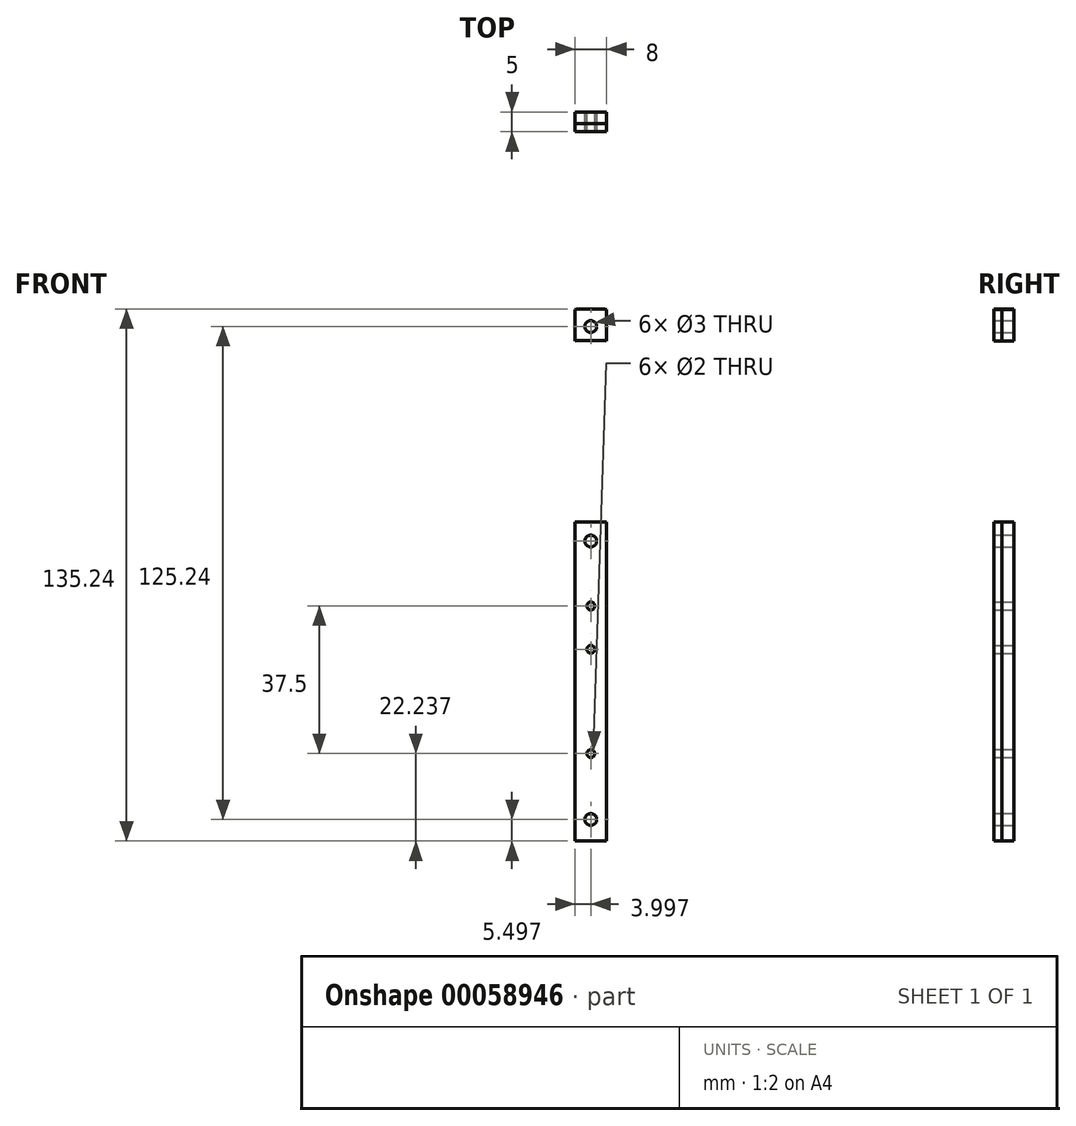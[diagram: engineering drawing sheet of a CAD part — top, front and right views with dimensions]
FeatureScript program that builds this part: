
annotation { "Feature Type Name" : "Feature", "Feature Type Description" : "" }
export const myFeature = defineFeature(function(context is Context, id is Id, definition is map)
    precondition{}
    {
        {
            var Q0;
            Q0=qCreatedBy(makeId("Front.planeOp"),FACE);
            var sketch = newSketch(context, id + "F0", { "sketchPlane" : qUnion([Q0])});
            skCircle(sketch, "E0", {"center": v(3.93, 28.4) * mm, "radius": 1.5 * mm});
            skLineSegment(sketch, "E1", {"start": v(7.05, 28.4) * mm, "end": v(-45.07, 28.4) * mm, "construction": true});
            skLineSegment(sketch, "E2", {"start": v(3.93, 33.22) * mm, "end": v(3.93, -47.83) * mm, "construction": true});
            skCircle(sketch, "E3", {"center": v(-34.07, 28.4) * mm, "radius": 1 * mm});
            skLineSegment(sketch, "E4", {"start": v(2.93, 11.9) * mm, "end": v(4.93, 11.9) * mm, "construction": true});
            skLineSegment(sketch, "E5", {"start": v(2.93, 0.9) * mm, "end": v(4.93, 0.9) * mm, "construction": true});
            skCircle(sketch, "E6", {"center": v(3.93, 0.9) * mm, "radius": 1 * mm});
            skLineSegment(sketch, "E7", {"start": v(2.93, -25.6) * mm, "end": v(4.93, -25.6) * mm, "construction": true});
            skCircle(sketch, "E8", {"center": v(3.93, -25.6) * mm, "radius": 1 * mm});
            skCircle(sketch, "E9", {"center": v(3.93, 11.9) * mm, "radius": 1 * mm});
            skPoint(sketch, "E10", {"position": v(3.93, -42.33) * mm});
            skCircle(sketch, "E11", {"center": v(3.93, -42.33) * mm, "radius": 1.5 * mm});
            skLineSegment(sketch, "E12.bottom", {"start": v(-0.07, 33.22) * mm, "end": v(7.93, 33.22) * mm});
            skLineSegment(sketch, "E12.top", {"start": v(-0.07, -47.83) * mm, "end": v(7.93, -47.83) * mm});
            skLineSegment(sketch, "E12.left", {"start": v(-0.07, 33.22) * mm, "end": v(-0.07, -47.83) * mm});
            skLineSegment(sketch, "E12.right", {"start": v(7.93, 33.22) * mm, "end": v(7.93, -47.83) * mm});
            skLineSegment(sketch, "E13.top", {"start": v(-0.07, 87.4) * mm, "end": v(7.93, 87.4) * mm});
            skLineSegment(sketch, "E13.left", {"start": v(-0.07, 33.22) * mm, "end": v(-0.07, 87.4) * mm});
            skLineSegment(sketch, "E13.right", {"start": v(7.93, 33.22) * mm, "end": v(7.93, 87.4) * mm});
            skPoint(sketch, "E14", {"position": v(3.93, 87.4) * mm});
            skCircle(sketch, "E15", {"center": v(3.93, 82.9) * mm, "radius": 1.5 * mm});
            skLineSegment(sketch, "E16", {"start": v(-0.07, 79.4) * mm, "end": v(7.93, 79.4) * mm, "construction": true});
            skCircle(sketch, "E17", {"center": v(3.93, 28.4) * mm, "radius": 59 * mm});
            skLineSegment(sketch, "E18", {"start": v(-0.07, 23.6) * mm, "end": v(7.93, 23.6) * mm});
            skCircle(sketch, "E19", {"center": v(3.93, 28.4) * mm, "radius": 51 * mm});
            skLineSegment(sketch, "E20", {"start": v(-0.07, 33.22) * mm, "end": v(-54.88, 33.22) * mm});
            skLineSegment(sketch, "E21", {"start": v(-0.07, 23.6) * mm, "end": v(-54.88, 23.6) * mm});
            skLineSegment(sketch, "E22", {"start": v(7.93, 33.22) * mm, "end": v(62.73, 33.22) * mm});
            skLineSegment(sketch, "E23", {"start": v(7.93, 23.6) * mm, "end": v(62.73, 23.6) * mm});
            skCircle(sketch, "E24", {"center": v(3.93, 28.4) * mm, "radius": 54.5 * mm, "construction": true});
            skSolve(sketch);
        }
        {
            var Q0;
            Q0=makeQuery(id+"F0.imprint","IMPRINT",FACE,{"disambiguationData":[TD([[makeQuery(id+"F0.imprint","IMPRINT",EDGE,{"derivedFrom":sQuery(id+"F0.wireOp",EDGE,"E12.bottom")}),1.0]])]});
            var Q1;
            Q1=makeQuery(id+"F0.imprint","IMPRINT",FACE,{"disambiguationData":[TD([[makeQuery(id+"F0.imprint","IMPRINT",EDGE,{"derivedFrom":sQuery(id+"F0.wireOp",EDGE,"E0")}),-1.0]])]});
            var Q2;
            {var subQ0=sQuery(id+"F0.wireOp",EDGE,"7f7ee0fa-9136-45af-b123-a8f84c0e82f5.right");Q2=makeQuery(id+"F0.imprint","IMPRINT",FACE,{"disambiguationData":[TD([[makeQuery(id+"F0.imprint","IMPRINT",EDGE,{"derivedFrom":subQ0}),-1.0]])]});}
            var Q3;
            Q3=makeQuery(id+"F0.imprint","IMPRINT",FACE,{"disambiguationData":[TD([[makeQuery(id+"F0.imprint","IMPRINT",EDGE,{"derivedFrom":sQuery(id+"F0.wireOp",EDGE,"E6")}),-1.0]])]});
            var Q4;
            Q4=makeQuery(id+"F0.imprint","IMPRINT",FACE,{"disambiguationData":[TD([[makeQuery(id+"F0.imprint","IMPRINT",EDGE,{"derivedFrom":sQuery(id+"F0.wireOp",EDGE,"E15")}),-1.0]])]});
            var Q5;
            {var subQ0=sQuery(id+"F0.wireOp",EDGE,"E17");var subQ1=sQuery(id+"F0.wireOp",EDGE,"E12.left");var subQ2=makeQuery(id+"F0.imprint","INTERSECT",VERTEX,{"derivedFrom":[subQ1,subQ0]});Q5=makeQuery(id+"F0.imprint","IMPRINT",FACE,{"disambiguationData":[TD([[makeQuery(id+"F0.imprint","IMPRINT",EDGE,{"disambiguationData":[TD([[subQ2,1.0]])],"derivedFrom":subQ1}),1.0]])]});}
            var Q6;
            Q6=makeQuery(id+"F0.imprint","IMPRINT",FACE,{"disambiguationData":[TD([[makeQuery(id+"F0.imprint","IMPRINT",EDGE,{"derivedFrom":sQuery(id+"F0.wireOp",EDGE,"E8")}),-1.0]])]});
            var Q7;
            Q7=makeQuery(id+"F0.imprint","IMPRINT",FACE,{"disambiguationData":[TD([[makeQuery(id+"F0.imprint","IMPRINT",EDGE,{"derivedFrom":sQuery(id+"F0.wireOp",EDGE,"E11")}),-1.0]])]});
            extrude(context, id + "F1", {"entities" : qUnion([Q0, Q1, Q2, Q3, Q4, Q5, Q6, Q7]), "depth" : 5 * mm});
        }
        {
            var Q0;
            Q0=makeQuery(id+"F0.imprint","IMPRINT",FACE,{"disambiguationData":[TD([[makeQuery(id+"F0.imprint","IMPRINT",EDGE,{"derivedFrom":sQuery(id+"F0.wireOp",EDGE,"E6")}),-1.0]])]});
            var Q1;
            {var subQ0=sQuery(id+"F0.wireOp",EDGE,"E17");var subQ1=sQuery(id+"F0.wireOp",EDGE,"E12.left");var subQ2=makeQuery(id+"F0.imprint","INTERSECT",VERTEX,{"derivedFrom":[subQ1,subQ0]});Q1=makeQuery(id+"F0.imprint","IMPRINT",FACE,{"disambiguationData":[TD([[makeQuery(id+"F0.imprint","IMPRINT",EDGE,{"disambiguationData":[TD([[subQ2,1.0]])],"derivedFrom":subQ1}),1.0]])]});}
            var Q2;
            Q2=makeQuery(id+"F0.imprint","IMPRINT",FACE,{"disambiguationData":[TD([[makeQuery(id+"F0.imprint","IMPRINT",EDGE,{"derivedFrom":sQuery(id+"F0.wireOp",EDGE,"E8")}),-1.0]])]});
            var Q3;
            Q3=makeQuery(id+"F0.imprint","IMPRINT",FACE,{"disambiguationData":[TD([[makeQuery(id+"F0.imprint","IMPRINT",EDGE,{"derivedFrom":sQuery(id+"F0.wireOp",EDGE,"E11")}),-1.0]])]});
            var Q4;
            Q4=makeQuery(id+"F0.imprint","IMPRINT",FACE,{"disambiguationData":[TD([[makeQuery(id+"F0.imprint","IMPRINT",EDGE,{"derivedFrom":sQuery(id+"F0.wireOp",EDGE,"E0")}),-1.0]])]});
            var Q5;
            {var subQ0=sQuery(id+"F0.wireOp",EDGE,"E12.bottom");Q5=makeQuery(id+"F0.imprint","IMPRINT",FACE,{"disambiguationData":[TD([[makeQuery(id+"F0.imprint","IMPRINT",EDGE,{"derivedFrom":subQ0}),1.0]])]});}
            var Q6;
            Q6=makeQuery(id+"F0.imprint","IMPRINT",FACE,{"disambiguationData":[TD([[makeQuery(id+"F0.imprint","IMPRINT",EDGE,{"derivedFrom":sQuery(id+"F0.wireOp",EDGE,"E15")}),-1.0]])]});
            extrude(context, id + "F2", {"entities" : qUnion([Q0, Q1, Q2, Q3, Q4, Q5, Q6]), "depth" : 3 * mm});
        }
    });
